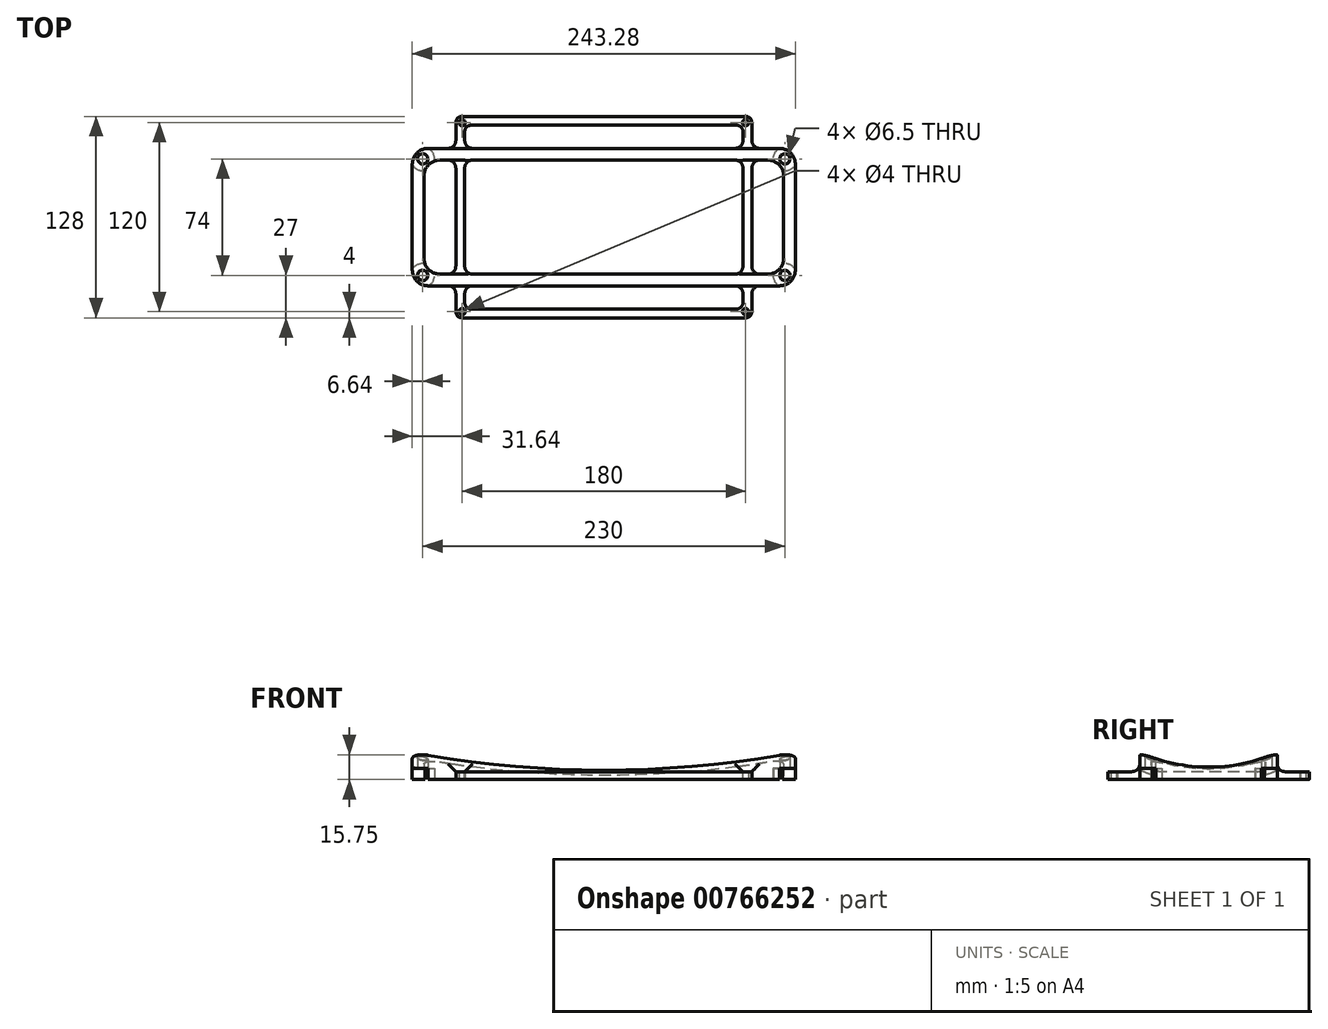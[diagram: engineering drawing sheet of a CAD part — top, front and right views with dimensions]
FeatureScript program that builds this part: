
annotation { "Feature Type Name" : "Feature", "Feature Type Description" : "" }
export const myFeature = defineFeature(function(context is Context, id is Id, definition is map)
    precondition{}
    {
        {
            var Q0;
            Q0=qCreatedBy(makeId("Top.planeOp"),FACE);
            var sketch = newSketch(context, id + "F0", { "sketchPlane" : qUnion([Q0])});
            skLineSegment(sketch, "E0.bottom", {"start": v(115, -37) * mm, "end": v(-115, -37) * mm, "construction": true});
            skLineSegment(sketch, "E0.top", {"start": v(115, 37) * mm, "end": v(-115, 37) * mm, "construction": true});
            skLineSegment(sketch, "E0.left", {"start": v(115, -37) * mm, "end": v(115, 37) * mm, "construction": true});
            skLineSegment(sketch, "E0.right", {"start": v(-115, -37) * mm, "end": v(-115, 37) * mm, "construction": true});
            skPoint(sketch, "E0.middle", {"position": v(0, 0) * mm});
            skCircle(sketch, "E1", {"center": v(-115, 37) * mm, "radius": 3.25 * mm});
            skCircle(sketch, "E2", {"center": v(115, 37) * mm, "radius": 3.25 * mm});
            skCircle(sketch, "E3", {"center": v(115, -37) * mm, "radius": 3.25 * mm});
            skCircle(sketch, "E4", {"center": v(-115, -37) * mm, "radius": 3.25 * mm});
            skLineSegment(sketch, "E5.bottom", {"start": v(104.22, 36.22) * mm, "end": v(-104.22, 36.22) * mm});
            skLineSegment(sketch, "E5.top", {"start": v(104.22, -36.22) * mm, "end": v(-104.22, -36.22) * mm});
            skLineSegment(sketch, "E5.left", {"start": v(114.22, 26.22) * mm, "end": v(114.22, -26.22) * mm});
            skLineSegment(sketch, "E5.right", {"start": v(-114.22, 26.22) * mm, "end": v(-114.22, -26.22) * mm});
            skPoint(sketch, "E6.visualSharp", {"position": v(-114.22, 36.22) * mm});
            skArc(sketch, "E6.filletArc", {"start": v(-104.22, 36.22) * mm, "mid": v(-111.29, 33.29) * mm, "end": v(-114.22, 26.22) * mm});
            skPoint(sketch, "E7.visualSharp", {"position": v(114.22, 36.22) * mm});
            skArc(sketch, "E7.filletArc", {"start": v(114.22, 26.22) * mm, "mid": v(111.29, 33.29) * mm, "end": v(104.22, 36.22) * mm});
            skPoint(sketch, "E8.visualSharp", {"position": v(114.22, -36.22) * mm});
            skArc(sketch, "E8.filletArc", {"start": v(104.22, -36.22) * mm, "mid": v(111.29, -33.29) * mm, "end": v(114.22, -26.22) * mm});
            skPoint(sketch, "E9.visualSharp", {"position": v(-114.22, -36.22) * mm});
            skArc(sketch, "E9.filletArc", {"start": v(-114.22, -26.22) * mm, "mid": v(-111.29, -33.29) * mm, "end": v(-104.22, -36.22) * mm});
            skLineSegment(sketch, "E10", {"start": v(-122.6, 44.6) * mm, "end": v(-95.21, 17.21) * mm, "construction": true});
            skLineSegment(sketch, "E11.bottom", {"start": v(111.64, 43.64) * mm, "end": v(-111.64, 43.64) * mm});
            skLineSegment(sketch, "E11.top", {"start": v(111.64, -43.64) * mm, "end": v(-111.64, -43.64) * mm});
            skLineSegment(sketch, "E11.left", {"start": v(121.64, 33.64) * mm, "end": v(121.64, -33.64) * mm});
            skLineSegment(sketch, "E11.right", {"start": v(-121.64, 33.64) * mm, "end": v(-121.64, -33.64) * mm});
            skPoint(sketch, "E12.visualSharp", {"position": v(-121.64, 43.64) * mm});
            skArc(sketch, "E12.filletArc", {"start": v(-111.64, 43.64) * mm, "mid": v(-118.71, 40.71) * mm, "end": v(-121.64, 33.64) * mm});
            skPoint(sketch, "E13.visualSharp", {"position": v(121.64, 43.64) * mm});
            skArc(sketch, "E13.filletArc", {"start": v(121.64, 33.64) * mm, "mid": v(118.71, 40.71) * mm, "end": v(111.64, 43.64) * mm});
            skPoint(sketch, "E14.visualSharp", {"position": v(121.64, -43.64) * mm});
            skArc(sketch, "E14.filletArc", {"start": v(111.64, -43.64) * mm, "mid": v(118.71, -40.71) * mm, "end": v(121.64, -33.64) * mm});
            skPoint(sketch, "E15.visualSharp", {"position": v(-121.64, -43.64) * mm});
            skArc(sketch, "E15.filletArc", {"start": v(-121.64, -33.64) * mm, "mid": v(-118.71, -40.71) * mm, "end": v(-111.64, -43.64) * mm});
            skSolve(sketch);
        }
        {
            var Q0;
            Q0=makeQuery(id+"F0.imprint","IMPRINT",FACE,{"disambiguationData":[TD([[makeQuery(id+"F0.imprint","IMPRINT",EDGE,{"derivedFrom":sQuery(id+"F0.wireOp",EDGE,"E1")}),-1.0]])]});
            extrude(context, id + "F1", {"entities" : qUnion([Q0]), "depth" : 18 * mm, "offsetDistance" : 25 * mm});
        }
        {
            var Q0;
            Q0=qCreatedBy(makeId("Right.planeOp"),FACE);
            var sketch = newSketch(context, id + "F2", { "sketchPlane" : qUnion([Q0])});
            skArc(sketch, "E16", {"start": v(-45.64, 6.82) * mm, "mid": v(0, -3.24) * mm, "end": v(45.64, 6.82) * mm});
            skLineSegment(sketch, "E17", {"start": v(-59.54, 666.25) * mm, "end": v(49.24, 666.25) * mm, "construction": true});
            skArc(sketch, "E18.0", {"start": v(-45.64, 23.65) * mm, "mid": v(0, 11.76) * mm, "end": v(45.64, 23.65) * mm});
            skLineSegment(sketch, "E19", {"start": v(-45.64, 6.82) * mm, "end": v(-45.64, 23.65) * mm});
            skLineSegment(sketch, "E20", {"start": v(45.64, 6.82) * mm, "end": v(45.64, 23.65) * mm});
            skPoint(sketch, "E21.0", {"position": v(33.64, 0) * mm});
            skSolve(sketch);
        }
        {
            var Q0;
            Q0 = qSketchRegion(id + "F2", true);
            var Q1;
            Q1=sQuery(id+"F2.wireOp",EDGE,"E17");
            revolve(context, id + "F3", {"operationType" : NewBodyOperationType.REMOVE, "surfaceOperationType" : NewSurfaceOperationType.NEW, "entities" : qUnion([Q0]), "axis" : qUnion([Q1]), "revolveType" : RevolveType.FULL, "oppositeDirection" : true});
        }
        {
            var Q0;
            Q0=qCreatedBy(makeId("Top.planeOp"),FACE);
            var sketch = newSketch(context, id + "F4", { "sketchPlane" : qUnion([Q0])});
            skLineSegment(sketch, "E22.bottom", {"start": v(90, -60) * mm, "end": v(-90, -60) * mm, "construction": true});
            skLineSegment(sketch, "E22.top", {"start": v(90, 60) * mm, "end": v(-90, 60) * mm, "construction": true});
            skLineSegment(sketch, "E22.left", {"start": v(90, -60) * mm, "end": v(90, 60) * mm, "construction": true});
            skLineSegment(sketch, "E22.right", {"start": v(-90, -60) * mm, "end": v(-90, 60) * mm, "construction": true});
            skPoint(sketch, "E22.middle", {"position": v(0, 0) * mm});
            skCircle(sketch, "E23", {"center": v(-90, 60) * mm, "radius": 2 * mm});
            skCircle(sketch, "E24", {"center": v(90, 60) * mm, "radius": 2 * mm});
            skCircle(sketch, "E25", {"center": v(90, -60) * mm, "radius": 2 * mm});
            skCircle(sketch, "E26", {"center": v(-90, -60) * mm, "radius": 2 * mm});
            skArc(sketch, "E27", {"start": v(94, 60) * mm, "mid": v(92.83, 62.83) * mm, "end": v(90, 64) * mm});
            skArc(sketch, "E28", {"start": v(90, -64) * mm, "mid": v(92.83, -62.83) * mm, "end": v(94, -60) * mm});
            skArc(sketch, "E29", {"start": v(-94, -60) * mm, "mid": v(-92.83, -62.83) * mm, "end": v(-90, -64) * mm});
            skArc(sketch, "E30", {"start": v(-90, 64) * mm, "mid": v(-92.83, 62.83) * mm, "end": v(-94, 60) * mm});
            skLineSegment(sketch, "E31", {"start": v(-90, 64) * mm, "end": v(90, 64) * mm});
            skLineSegment(sketch, "E32", {"start": v(-94, 60) * mm, "end": v(-94, -60) * mm});
            skLineSegment(sketch, "E33", {"start": v(-90, -64) * mm, "end": v(90, -64) * mm});
            skLineSegment(sketch, "E34", {"start": v(94, -60) * mm, "end": v(94, 60) * mm});
            skLineSegment(sketch, "E35.bottom", {"start": v(84.34, 58.34) * mm, "end": v(-84.34, 58.34) * mm});
            skLineSegment(sketch, "E35.top", {"start": v(84.34, -58.34) * mm, "end": v(-84.34, -58.34) * mm});
            skLineSegment(sketch, "E35.left", {"start": v(88.34, 54.34) * mm, "end": v(88.34, -54.34) * mm});
            skLineSegment(sketch, "E35.right", {"start": v(-88.34, 54.34) * mm, "end": v(-88.34, -54.34) * mm});
            skPoint(sketch, "E36.visualSharp", {"position": v(-88.34, 58.34) * mm});
            skArc(sketch, "E36.filletArc", {"start": v(-84.34, 58.34) * mm, "mid": v(-87.17, 57.17) * mm, "end": v(-88.34, 54.34) * mm});
            skPoint(sketch, "E37.visualSharp", {"position": v(88.34, 58.34) * mm});
            skArc(sketch, "E37.filletArc", {"start": v(88.34, 54.34) * mm, "mid": v(87.17, 57.17) * mm, "end": v(84.34, 58.34) * mm});
            skPoint(sketch, "E38.visualSharp", {"position": v(88.34, -58.34) * mm});
            skArc(sketch, "E38.filletArc", {"start": v(84.34, -58.34) * mm, "mid": v(87.17, -57.17) * mm, "end": v(88.34, -54.34) * mm});
            skPoint(sketch, "E39.visualSharp", {"position": v(-88.34, -58.34) * mm});
            skArc(sketch, "E39.filletArc", {"start": v(-88.34, -54.34) * mm, "mid": v(-87.17, -57.17) * mm, "end": v(-84.34, -58.34) * mm});
            skLineSegment(sketch, "E40", {"start": v(-90, 60) * mm, "end": v(-51.44, 21.44) * mm, "construction": true});
            skSolve(sketch);
        }
        {
            var Q0;
            Q0 = qSketchRegion(id + "F4", true);
            extrude(context, id + "F5", {"entities" : qUnion([Q0]), "operationType" : NewBodyOperationType.ADD, "depth" : 5 * mm, "offsetDistance" : 25 * mm});
        }
        {
            var Q0;
            Q0=makeQuery(id+"F5.boolean.opBoolean","INTERSECT",EDGE,{"derivedFrom":[makeQuery(id+"F1.opExtrude","SWEPT_FACE",FACE,{"disambiguationData":[OSD([sQuery(id+"F0.wireOp",EDGE,"E11.bottom")])]}),makeQuery(id+"F5.opExtrude","SWEPT_FACE",FACE,{"disambiguationData":[OSD([sQuery(id+"F4.wireOp",EDGE,"E34")])]})]});
            var Q1;
            Q1=makeQuery(id+"F5.boolean.opBoolean","INTERSECT",EDGE,{"derivedFrom":[makeQuery(id+"F1.opExtrude","SWEPT_FACE",FACE,{"disambiguationData":[OSD([sQuery(id+"F0.wireOp",EDGE,"E11.bottom")])]}),makeQuery(id+"F5.opExtrude","SWEPT_FACE",FACE,{"disambiguationData":[OSD([sQuery(id+"F4.wireOp",EDGE,"E35.left")])]})]});
            var Q2;
            Q2=makeQuery(id+"F5.boolean.opBoolean","INTERSECT",EDGE,{"disambiguationData":[OD(1.0)],"derivedFrom":[makeQuery(id+"F1.opExtrude","SWEPT_FACE",FACE,{"disambiguationData":[OSD([sQuery(id+"F0.wireOp",EDGE,"E11.bottom")])]}),makeQuery(id+"F5.opExtrude","CAP_FACE",FACE,{"disambiguationData":[OSD([sQuery(id+"F4.wireOp",EDGE,"E23"),sQuery(id+"F4.wireOp",EDGE,"E24"),sQuery(id+"F4.wireOp",EDGE,"E25"),sQuery(id+"F4.wireOp",EDGE,"E26"),sQuery(id+"F4.wireOp",EDGE,"E27"),sQuery(id+"F4.wireOp",EDGE,"E28"),sQuery(id+"F4.wireOp",EDGE,"E29"),sQuery(id+"F4.wireOp",EDGE,"E30"),sQuery(id+"F4.wireOp",EDGE,"E31"),sQuery(id+"F4.wireOp",EDGE,"E32"),sQuery(id+"F4.wireOp",EDGE,"E33"),sQuery(id+"F4.wireOp",EDGE,"E34"),sQuery(id+"F4.wireOp",EDGE,"E35.bottom"),sQuery(id+"F4.wireOp",EDGE,"E35.top"),sQuery(id+"F4.wireOp",EDGE,"E35.left"),sQuery(id+"F4.wireOp",EDGE,"E35.right"),sQuery(id+"F4.wireOp",EDGE,"E36.filletArc"),sQuery(id+"F4.wireOp",EDGE,"E37.filletArc"),sQuery(id+"F4.wireOp",EDGE,"E38.filletArc"),sQuery(id+"F4.wireOp",EDGE,"E39.filletArc")])],"isStart":false})]});
            var Q3;
            Q3=makeQuery(id+"F5.boolean.opBoolean","INTERSECT",EDGE,{"derivedFrom":[makeQuery(id+"F1.opExtrude","SWEPT_FACE",FACE,{"disambiguationData":[OSD([sQuery(id+"F0.wireOp",EDGE,"E11.bottom")])]}),makeQuery(id+"F5.opExtrude","SWEPT_FACE",FACE,{"disambiguationData":[OSD([sQuery(id+"F4.wireOp",EDGE,"E32")])]})]});
            var Q4;
            Q4=makeQuery(id+"F5.boolean.opBoolean","INTERSECT",EDGE,{"derivedFrom":[makeQuery(id+"F1.opExtrude","SWEPT_FACE",FACE,{"disambiguationData":[OSD([sQuery(id+"F0.wireOp",EDGE,"E11.bottom")])]}),makeQuery(id+"F5.opExtrude","SWEPT_FACE",FACE,{"disambiguationData":[OSD([sQuery(id+"F4.wireOp",EDGE,"E35.right")])]})]});
            var Q5;
            Q5=makeQuery(id+"F5.boolean.opBoolean","INTERSECT",EDGE,{"disambiguationData":[OD(0.0)],"derivedFrom":[makeQuery(id+"F1.opExtrude","SWEPT_FACE",FACE,{"disambiguationData":[OSD([sQuery(id+"F0.wireOp",EDGE,"E11.bottom")])]}),makeQuery(id+"F5.opExtrude","CAP_FACE",FACE,{"disambiguationData":[OSD([sQuery(id+"F4.wireOp",EDGE,"E23"),sQuery(id+"F4.wireOp",EDGE,"E24"),sQuery(id+"F4.wireOp",EDGE,"E25"),sQuery(id+"F4.wireOp",EDGE,"E26"),sQuery(id+"F4.wireOp",EDGE,"E27"),sQuery(id+"F4.wireOp",EDGE,"E28"),sQuery(id+"F4.wireOp",EDGE,"E29"),sQuery(id+"F4.wireOp",EDGE,"E30"),sQuery(id+"F4.wireOp",EDGE,"E31"),sQuery(id+"F4.wireOp",EDGE,"E32"),sQuery(id+"F4.wireOp",EDGE,"E33"),sQuery(id+"F4.wireOp",EDGE,"E34"),sQuery(id+"F4.wireOp",EDGE,"E35.bottom"),sQuery(id+"F4.wireOp",EDGE,"E35.top"),sQuery(id+"F4.wireOp",EDGE,"E35.left"),sQuery(id+"F4.wireOp",EDGE,"E35.right"),sQuery(id+"F4.wireOp",EDGE,"E36.filletArc"),sQuery(id+"F4.wireOp",EDGE,"E37.filletArc"),sQuery(id+"F4.wireOp",EDGE,"E38.filletArc"),sQuery(id+"F4.wireOp",EDGE,"E39.filletArc")])],"isStart":false})]});
            var Q6;
            Q6=makeQuery(id+"F5.boolean.opBoolean","INTERSECT",EDGE,{"derivedFrom":[makeQuery(id+"F1.opExtrude","SWEPT_FACE",FACE,{"disambiguationData":[OSD([sQuery(id+"F0.wireOp",EDGE,"E11.top")])]}),makeQuery(id+"F5.opExtrude","SWEPT_FACE",FACE,{"disambiguationData":[OSD([sQuery(id+"F4.wireOp",EDGE,"E32")])]})]});
            var Q7;
            Q7=makeQuery(id+"F5.boolean.opBoolean","INTERSECT",EDGE,{"disambiguationData":[OD(0.0)],"derivedFrom":[makeQuery(id+"F1.opExtrude","SWEPT_FACE",FACE,{"disambiguationData":[OSD([sQuery(id+"F0.wireOp",EDGE,"E11.top")])]}),makeQuery(id+"F5.opExtrude","CAP_FACE",FACE,{"disambiguationData":[OSD([sQuery(id+"F4.wireOp",EDGE,"E23"),sQuery(id+"F4.wireOp",EDGE,"E24"),sQuery(id+"F4.wireOp",EDGE,"E25"),sQuery(id+"F4.wireOp",EDGE,"E26"),sQuery(id+"F4.wireOp",EDGE,"E27"),sQuery(id+"F4.wireOp",EDGE,"E28"),sQuery(id+"F4.wireOp",EDGE,"E29"),sQuery(id+"F4.wireOp",EDGE,"E30"),sQuery(id+"F4.wireOp",EDGE,"E31"),sQuery(id+"F4.wireOp",EDGE,"E32"),sQuery(id+"F4.wireOp",EDGE,"E33"),sQuery(id+"F4.wireOp",EDGE,"E34"),sQuery(id+"F4.wireOp",EDGE,"E35.bottom"),sQuery(id+"F4.wireOp",EDGE,"E35.top"),sQuery(id+"F4.wireOp",EDGE,"E35.left"),sQuery(id+"F4.wireOp",EDGE,"E35.right"),sQuery(id+"F4.wireOp",EDGE,"E36.filletArc"),sQuery(id+"F4.wireOp",EDGE,"E37.filletArc"),sQuery(id+"F4.wireOp",EDGE,"E38.filletArc"),sQuery(id+"F4.wireOp",EDGE,"E39.filletArc")])],"isStart":false})]});
            var Q8;
            Q8=makeQuery(id+"F5.boolean.opBoolean","INTERSECT",EDGE,{"derivedFrom":[makeQuery(id+"F1.opExtrude","SWEPT_FACE",FACE,{"disambiguationData":[OSD([sQuery(id+"F0.wireOp",EDGE,"E11.top")])]}),makeQuery(id+"F5.opExtrude","SWEPT_FACE",FACE,{"disambiguationData":[OSD([sQuery(id+"F4.wireOp",EDGE,"E35.right")])]})]});
            var Q9;
            Q9=makeQuery(id+"F5.boolean.opBoolean","INTERSECT",EDGE,{"derivedFrom":[makeQuery(id+"F1.opExtrude","SWEPT_FACE",FACE,{"disambiguationData":[OSD([sQuery(id+"F0.wireOp",EDGE,"E11.top")])]}),makeQuery(id+"F5.opExtrude","SWEPT_FACE",FACE,{"disambiguationData":[OSD([sQuery(id+"F4.wireOp",EDGE,"E34")])]})]});
            var Q10;
            Q10=makeQuery(id+"F5.boolean.opBoolean","INTERSECT",EDGE,{"disambiguationData":[OD(1.0)],"derivedFrom":[makeQuery(id+"F1.opExtrude","SWEPT_FACE",FACE,{"disambiguationData":[OSD([sQuery(id+"F0.wireOp",EDGE,"E11.top")])]}),makeQuery(id+"F5.opExtrude","CAP_FACE",FACE,{"disambiguationData":[OSD([sQuery(id+"F4.wireOp",EDGE,"E23"),sQuery(id+"F4.wireOp",EDGE,"E24"),sQuery(id+"F4.wireOp",EDGE,"E25"),sQuery(id+"F4.wireOp",EDGE,"E26"),sQuery(id+"F4.wireOp",EDGE,"E27"),sQuery(id+"F4.wireOp",EDGE,"E28"),sQuery(id+"F4.wireOp",EDGE,"E29"),sQuery(id+"F4.wireOp",EDGE,"E30"),sQuery(id+"F4.wireOp",EDGE,"E31"),sQuery(id+"F4.wireOp",EDGE,"E32"),sQuery(id+"F4.wireOp",EDGE,"E33"),sQuery(id+"F4.wireOp",EDGE,"E34"),sQuery(id+"F4.wireOp",EDGE,"E35.bottom"),sQuery(id+"F4.wireOp",EDGE,"E35.top"),sQuery(id+"F4.wireOp",EDGE,"E35.left"),sQuery(id+"F4.wireOp",EDGE,"E35.right"),sQuery(id+"F4.wireOp",EDGE,"E36.filletArc"),sQuery(id+"F4.wireOp",EDGE,"E37.filletArc"),sQuery(id+"F4.wireOp",EDGE,"E38.filletArc"),sQuery(id+"F4.wireOp",EDGE,"E39.filletArc")])],"isStart":false})]});
            var Q11;
            Q11=makeQuery(id+"F5.boolean.opBoolean","INTERSECT",EDGE,{"derivedFrom":[makeQuery(id+"F1.opExtrude","SWEPT_FACE",FACE,{"disambiguationData":[OSD([sQuery(id+"F0.wireOp",EDGE,"E11.top")])]}),makeQuery(id+"F5.opExtrude","SWEPT_FACE",FACE,{"disambiguationData":[OSD([sQuery(id+"F4.wireOp",EDGE,"E35.left")])]})]});
            var Q12;
            Q12=makeQuery(id+"F5.boolean.opBoolean","INTERSECT",EDGE,{"derivedFrom":[makeQuery(id+"F1.opExtrude","SWEPT_FACE",FACE,{"disambiguationData":[OSD([sQuery(id+"F0.wireOp",EDGE,"E5.bottom")])]}),makeQuery(id+"F5.opExtrude","SWEPT_FACE",FACE,{"disambiguationData":[OSD([sQuery(id+"F4.wireOp",EDGE,"E32")])]})]});
            var Q13;
            Q13=makeQuery(id+"F5.boolean.opBoolean","INTERSECT",EDGE,{"disambiguationData":[OD(0.0)],"derivedFrom":[makeQuery(id+"F1.opExtrude","SWEPT_FACE",FACE,{"disambiguationData":[OSD([sQuery(id+"F0.wireOp",EDGE,"E5.bottom")])]}),makeQuery(id+"F5.opExtrude","CAP_FACE",FACE,{"disambiguationData":[OSD([sQuery(id+"F4.wireOp",EDGE,"E23"),sQuery(id+"F4.wireOp",EDGE,"E24"),sQuery(id+"F4.wireOp",EDGE,"E25"),sQuery(id+"F4.wireOp",EDGE,"E26"),sQuery(id+"F4.wireOp",EDGE,"E27"),sQuery(id+"F4.wireOp",EDGE,"E28"),sQuery(id+"F4.wireOp",EDGE,"E29"),sQuery(id+"F4.wireOp",EDGE,"E30"),sQuery(id+"F4.wireOp",EDGE,"E31"),sQuery(id+"F4.wireOp",EDGE,"E32"),sQuery(id+"F4.wireOp",EDGE,"E33"),sQuery(id+"F4.wireOp",EDGE,"E34"),sQuery(id+"F4.wireOp",EDGE,"E35.bottom"),sQuery(id+"F4.wireOp",EDGE,"E35.top"),sQuery(id+"F4.wireOp",EDGE,"E35.left"),sQuery(id+"F4.wireOp",EDGE,"E35.right"),sQuery(id+"F4.wireOp",EDGE,"E36.filletArc"),sQuery(id+"F4.wireOp",EDGE,"E37.filletArc"),sQuery(id+"F4.wireOp",EDGE,"E38.filletArc"),sQuery(id+"F4.wireOp",EDGE,"E39.filletArc")])],"isStart":false})]});
            var Q14;
            Q14=makeQuery(id+"F5.boolean.opBoolean","INTERSECT",EDGE,{"derivedFrom":[makeQuery(id+"F1.opExtrude","SWEPT_FACE",FACE,{"disambiguationData":[OSD([sQuery(id+"F0.wireOp",EDGE,"E5.bottom")])]}),makeQuery(id+"F5.opExtrude","SWEPT_FACE",FACE,{"disambiguationData":[OSD([sQuery(id+"F4.wireOp",EDGE,"E35.right")])]})]});
            var Q15;
            Q15=makeQuery(id+"F5.boolean.opBoolean","INTERSECT",EDGE,{"derivedFrom":[makeQuery(id+"F1.opExtrude","SWEPT_FACE",FACE,{"disambiguationData":[OSD([sQuery(id+"F0.wireOp",EDGE,"E5.top")])]}),makeQuery(id+"F5.opExtrude","SWEPT_FACE",FACE,{"disambiguationData":[OSD([sQuery(id+"F4.wireOp",EDGE,"E35.left")])]})]});
            var Q16;
            Q16=makeQuery(id+"F5.boolean.opBoolean","INTERSECT",EDGE,{"disambiguationData":[OD(1.0)],"derivedFrom":[makeQuery(id+"F1.opExtrude","SWEPT_FACE",FACE,{"disambiguationData":[OSD([sQuery(id+"F0.wireOp",EDGE,"E5.top")])]}),makeQuery(id+"F5.opExtrude","CAP_FACE",FACE,{"disambiguationData":[OSD([sQuery(id+"F4.wireOp",EDGE,"E23"),sQuery(id+"F4.wireOp",EDGE,"E24"),sQuery(id+"F4.wireOp",EDGE,"E25"),sQuery(id+"F4.wireOp",EDGE,"E26"),sQuery(id+"F4.wireOp",EDGE,"E27"),sQuery(id+"F4.wireOp",EDGE,"E28"),sQuery(id+"F4.wireOp",EDGE,"E29"),sQuery(id+"F4.wireOp",EDGE,"E30"),sQuery(id+"F4.wireOp",EDGE,"E31"),sQuery(id+"F4.wireOp",EDGE,"E32"),sQuery(id+"F4.wireOp",EDGE,"E33"),sQuery(id+"F4.wireOp",EDGE,"E34"),sQuery(id+"F4.wireOp",EDGE,"E35.bottom"),sQuery(id+"F4.wireOp",EDGE,"E35.top"),sQuery(id+"F4.wireOp",EDGE,"E35.left"),sQuery(id+"F4.wireOp",EDGE,"E35.right"),sQuery(id+"F4.wireOp",EDGE,"E36.filletArc"),sQuery(id+"F4.wireOp",EDGE,"E37.filletArc"),sQuery(id+"F4.wireOp",EDGE,"E38.filletArc"),sQuery(id+"F4.wireOp",EDGE,"E39.filletArc")])],"isStart":false})]});
            var Q17;
            Q17=makeQuery(id+"F5.boolean.opBoolean","INTERSECT",EDGE,{"derivedFrom":[makeQuery(id+"F1.opExtrude","SWEPT_FACE",FACE,{"disambiguationData":[OSD([sQuery(id+"F0.wireOp",EDGE,"E5.top")])]}),makeQuery(id+"F5.opExtrude","SWEPT_FACE",FACE,{"disambiguationData":[OSD([sQuery(id+"F4.wireOp",EDGE,"E34")])]})]});
            var Q18;
            Q18=makeQuery(id+"F5.boolean.opBoolean","INTERSECT",EDGE,{"derivedFrom":[makeQuery(id+"F1.opExtrude","SWEPT_FACE",FACE,{"disambiguationData":[OSD([sQuery(id+"F0.wireOp",EDGE,"E5.bottom")])]}),makeQuery(id+"F5.opExtrude","SWEPT_FACE",FACE,{"disambiguationData":[OSD([sQuery(id+"F4.wireOp",EDGE,"E35.left")])]})]});
            var Q19;
            Q19=makeQuery(id+"F5.boolean.opBoolean","INTERSECT",EDGE,{"disambiguationData":[OD(1.0)],"derivedFrom":[makeQuery(id+"F1.opExtrude","SWEPT_FACE",FACE,{"disambiguationData":[OSD([sQuery(id+"F0.wireOp",EDGE,"E5.bottom")])]}),makeQuery(id+"F5.opExtrude","CAP_FACE",FACE,{"disambiguationData":[OSD([sQuery(id+"F4.wireOp",EDGE,"E23"),sQuery(id+"F4.wireOp",EDGE,"E24"),sQuery(id+"F4.wireOp",EDGE,"E25"),sQuery(id+"F4.wireOp",EDGE,"E26"),sQuery(id+"F4.wireOp",EDGE,"E27"),sQuery(id+"F4.wireOp",EDGE,"E28"),sQuery(id+"F4.wireOp",EDGE,"E29"),sQuery(id+"F4.wireOp",EDGE,"E30"),sQuery(id+"F4.wireOp",EDGE,"E31"),sQuery(id+"F4.wireOp",EDGE,"E32"),sQuery(id+"F4.wireOp",EDGE,"E33"),sQuery(id+"F4.wireOp",EDGE,"E34"),sQuery(id+"F4.wireOp",EDGE,"E35.bottom"),sQuery(id+"F4.wireOp",EDGE,"E35.top"),sQuery(id+"F4.wireOp",EDGE,"E35.left"),sQuery(id+"F4.wireOp",EDGE,"E35.right"),sQuery(id+"F4.wireOp",EDGE,"E36.filletArc"),sQuery(id+"F4.wireOp",EDGE,"E37.filletArc"),sQuery(id+"F4.wireOp",EDGE,"E38.filletArc"),sQuery(id+"F4.wireOp",EDGE,"E39.filletArc")])],"isStart":false})]});
            var Q20;
            Q20=makeQuery(id+"F5.boolean.opBoolean","INTERSECT",EDGE,{"derivedFrom":[makeQuery(id+"F1.opExtrude","SWEPT_FACE",FACE,{"disambiguationData":[OSD([sQuery(id+"F0.wireOp",EDGE,"E5.bottom")])]}),makeQuery(id+"F5.opExtrude","SWEPT_FACE",FACE,{"disambiguationData":[OSD([sQuery(id+"F4.wireOp",EDGE,"E34")])]})]});
            var Q21;
            Q21=makeQuery(id+"F5.boolean.opBoolean","INTERSECT",EDGE,{"derivedFrom":[makeQuery(id+"F1.opExtrude","SWEPT_FACE",FACE,{"disambiguationData":[OSD([sQuery(id+"F0.wireOp",EDGE,"E5.top")])]}),makeQuery(id+"F5.opExtrude","SWEPT_FACE",FACE,{"disambiguationData":[OSD([sQuery(id+"F4.wireOp",EDGE,"E32")])]})]});
            var Q22;
            Q22=makeQuery(id+"F5.boolean.opBoolean","INTERSECT",EDGE,{"disambiguationData":[OD(0.0)],"derivedFrom":[makeQuery(id+"F1.opExtrude","SWEPT_FACE",FACE,{"disambiguationData":[OSD([sQuery(id+"F0.wireOp",EDGE,"E5.top")])]}),makeQuery(id+"F5.opExtrude","CAP_FACE",FACE,{"disambiguationData":[OSD([sQuery(id+"F4.wireOp",EDGE,"E23"),sQuery(id+"F4.wireOp",EDGE,"E24"),sQuery(id+"F4.wireOp",EDGE,"E25"),sQuery(id+"F4.wireOp",EDGE,"E26"),sQuery(id+"F4.wireOp",EDGE,"E27"),sQuery(id+"F4.wireOp",EDGE,"E28"),sQuery(id+"F4.wireOp",EDGE,"E29"),sQuery(id+"F4.wireOp",EDGE,"E30"),sQuery(id+"F4.wireOp",EDGE,"E31"),sQuery(id+"F4.wireOp",EDGE,"E32"),sQuery(id+"F4.wireOp",EDGE,"E33"),sQuery(id+"F4.wireOp",EDGE,"E34"),sQuery(id+"F4.wireOp",EDGE,"E35.bottom"),sQuery(id+"F4.wireOp",EDGE,"E35.top"),sQuery(id+"F4.wireOp",EDGE,"E35.left"),sQuery(id+"F4.wireOp",EDGE,"E35.right"),sQuery(id+"F4.wireOp",EDGE,"E36.filletArc"),sQuery(id+"F4.wireOp",EDGE,"E37.filletArc"),sQuery(id+"F4.wireOp",EDGE,"E38.filletArc"),sQuery(id+"F4.wireOp",EDGE,"E39.filletArc")])],"isStart":false})]});
            var Q23;
            Q23=makeQuery(id+"F5.boolean.opBoolean","INTERSECT",EDGE,{"derivedFrom":[makeQuery(id+"F1.opExtrude","SWEPT_FACE",FACE,{"disambiguationData":[OSD([sQuery(id+"F0.wireOp",EDGE,"E5.top")])]}),makeQuery(id+"F5.opExtrude","SWEPT_FACE",FACE,{"disambiguationData":[OSD([sQuery(id+"F4.wireOp",EDGE,"E35.right")])]})]});
            fillet(context, id + "F6", {"entities" : qUnion([Q0, Q1, Q2, Q3, Q4, Q5, Q6, Q7, Q8, Q9, Q10, Q11, Q12, Q13, Q14, Q15, Q16, Q17, Q18, Q19, Q20, Q21, Q22, Q23]), "radius" : 5 * mm, "tangentPropagation" : true, "allowEdgeOverflow" : false});
        }
        {
            var Q0;
            Q0=qCreatedBy(makeId("Top.planeOp"),FACE);
            var sketch = newSketch(context, id + "F7", { "sketchPlane" : qUnion([Q0])});
            skCircle(sketch, "E41.0", {"center": v(-115, -37) * mm, "radius": 3.25 * mm, "construction": true});
            skCircle(sketch, "E42.0", {"center": v(-115, 37) * mm, "radius": 3.25 * mm, "construction": true});
            skCircle(sketch, "E43.0", {"center": v(115, 37) * mm, "radius": 3.25 * mm, "construction": true});
            skCircle(sketch, "E44.0", {"center": v(115, -37) * mm, "radius": 3.25 * mm, "construction": true});
            skCircle(sketch, "E45", {"center": v(-115, -37) * mm, "radius": 7.5 * mm});
            skCircle(sketch, "E46", {"center": v(115, -37) * mm, "radius": 7.5 * mm});
            skCircle(sketch, "E47", {"center": v(115, 37) * mm, "radius": 7.5 * mm});
            skCircle(sketch, "E48", {"center": v(-115, 37) * mm, "radius": 7.5 * mm});
            skSolve(sketch);
        }
        {
            var Q0;
            Q0 = qSketchRegion(id + "F7", true);
            extrude(context, id + "F8", {"entities" : qUnion([Q0]), "operationType" : NewBodyOperationType.REMOVE, "depth" : 7 * mm, "offsetDistance" : 25 * mm});
        }
    });
